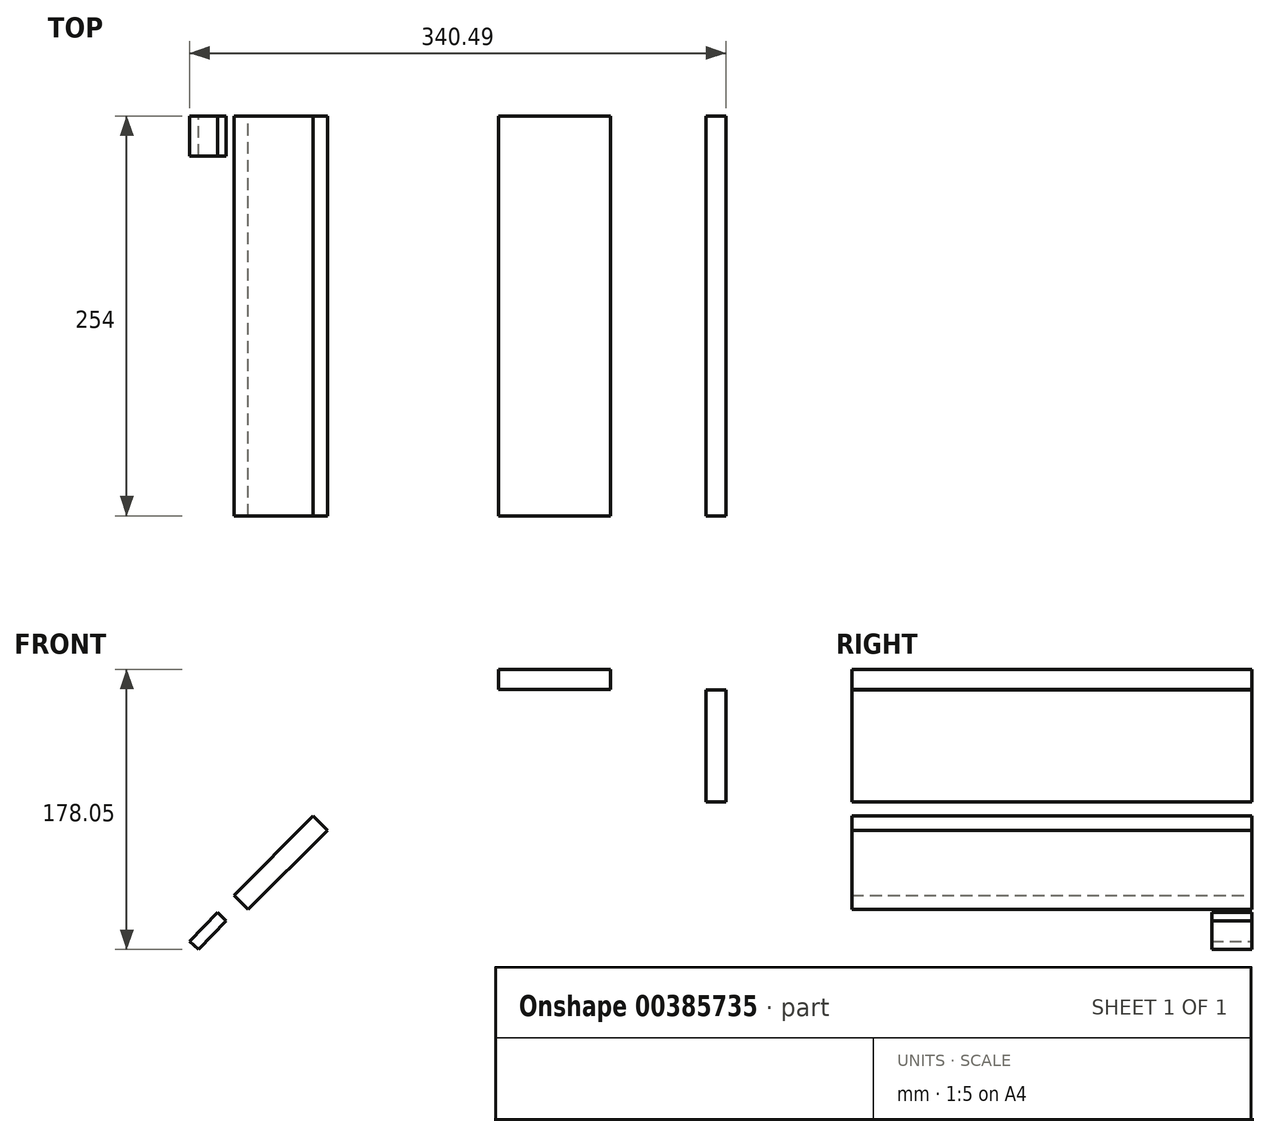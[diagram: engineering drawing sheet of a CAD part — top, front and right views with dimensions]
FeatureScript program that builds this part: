
annotation { "Feature Type Name" : "Feature", "Feature Type Description" : "" }
export const myFeature = defineFeature(function(context is Context, id is Id, definition is map)
    precondition{}
    {
        {
            var Q0;
            Q0=qCreatedBy(makeId("Front.planeOp"),FACE);
            var sketch = newSketch(context, id + "F0", { "sketchPlane" : qUnion([Q0])});
            skLineSegment(sketch, "E0", {"start": v(-27.4, 174.52) * mm, "end": v(43.71, 174.52) * mm});
            skLineSegment(sketch, "E1", {"start": v(43.71, 174.52) * mm, "end": v(43.71, 187.22) * mm});
            skLineSegment(sketch, "E2", {"start": v(43.71, 187.22) * mm, "end": v(-27.4, 187.22) * mm});
            skLineSegment(sketch, "E3", {"start": v(-27.4, 187.22) * mm, "end": v(-27.4, 174.52) * mm});
            skLineSegment(sketch, "E4", {"start": v(104.33, 174.13) * mm, "end": v(104.33, 103.01) * mm});
            skLineSegment(sketch, "E5", {"start": v(104.33, 103.01) * mm, "end": v(117.03, 103.01) * mm});
            skLineSegment(sketch, "E6", {"start": v(117.03, 103.01) * mm, "end": v(117.03, 174.13) * mm});
            skLineSegment(sketch, "E7", {"start": v(117.03, 174.13) * mm, "end": v(104.33, 174.13) * mm});
            skLineSegment(sketch, "E8", {"start": v(-186.28, 34.67) * mm, "end": v(-136, 84.95) * mm});
            skLineSegment(sketch, "E9", {"start": v(-136, 84.95) * mm, "end": v(-144.97, 93.94) * mm});
            skLineSegment(sketch, "E10", {"start": v(-144.97, 93.94) * mm, "end": v(-195.26, 43.65) * mm});
            skLineSegment(sketch, "E11", {"start": v(-195.26, 43.65) * mm, "end": v(-186.28, 34.67) * mm});
            skSolve(sketch);
        }
        {
            var Q0;
            Q0=qSketchRegion(id+"F0",true);
            extrude(context, id + "F1", {"entities" : qUnion([Q0]), "depth" : 254 * mm});
        }
        {
            var Q0;
            Q0=qCreatedBy(makeId("Front.planeOp"),FACE);
            var sketch = newSketch(context, id + "F2", { "sketchPlane" : qUnion([Q0])});
            skLineSegment(sketch, "E12", {"start": v(-217.98, 9.17) * mm, "end": v(-200.33, 27.44) * mm});
            skLineSegment(sketch, "E13", {"start": v(-200.33, 27.44) * mm, "end": v(-205.81, 32.74) * mm});
            skLineSegment(sketch, "E14", {"start": v(-205.81, 32.74) * mm, "end": v(-223.46, 14.46) * mm});
            skLineSegment(sketch, "E15", {"start": v(-223.46, 14.46) * mm, "end": v(-217.98, 9.17) * mm});
            skSolve(sketch);
        }
        {
            var Q0;
            Q0=makeQuery(id+"F2.imprint","IMPRINT",FACE,{"disambiguationData":[TD([[makeQuery(id+"F2.imprint","IMPRINT",EDGE,{"derivedFrom":sQuery(id+"F2.wireOp",EDGE,"E12")}),1.0]])]});
            extrude(context, id + "F3", {"entities" : qUnion([Q0]), "depth" : 25.4 * mm});
        }
    });
